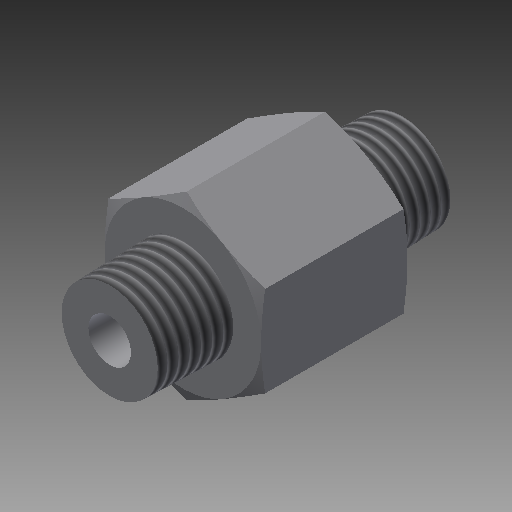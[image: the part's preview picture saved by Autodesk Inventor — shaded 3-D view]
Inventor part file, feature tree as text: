
AUTODESK INVENTOR PART (.ipt)
format: ipt  version: 2017 (Build 210142000, 142)  size: 175,104 bytes
history: native  units: in
note: dims shown in document units (in); Inventor stores cm internally (conversion verified against a paired STEP export)
features: sketch x4, extrude x3, plane x2, thread x2, other x1, hole x1, revolve x1, mirror x1, reference x1
ambient origin geometry x8: Origin, YZ Plane, XZ Plane, XY Plane, X Axis, Y Axis, Z Axis, Center Point
bodies: Solid1 (feature_tree)
feature tree (16):
  sketch  "Sketch1"  dims[d2=0.5in d3=0.0in d20=0.25in d21=-0.0123in]
  extrude  "Extrusion1"  Depth=0.25in
  plane  "Work Plane1"
  other  "Work Axis3"
  extrude  "Extrusion3"  Depth=0.25in
  thread  "Thread2"  [1 undecoded]
  hole  "Hole2"  [1 undecoded]
  extrude  "Extrusion4"  Depth=0.0414in
  thread  "Thread3"  [1 undecoded]
  revolve  "Revolution3"  [1 undecoded]
  plane  "Work Plane4"
  mirror  "Mirror4"
  sketch  "Sketch6"  dims[d22=0.392in d23=0.0in]
  reference  "Reference3"
  sketch  "Sketch7"  dims[d24=0.13in d25=0.75in d26=0.375in d27=0.25in d28=0.5635in d29=1.0in d30=0.8108in d31=0.25in d32=-0.0123in d33=0.392in d34=0.0in]
  sketch  "Sketch8"  dims[d35=90.0deg d36=0.5355in d37=0.0414in d38=0.0415in]
note: 4 required parameter values undecoded (feature->parameter linkage not recoverable at this tier; creation-order binding heuristic only, values carry confidence <= 0.55)
